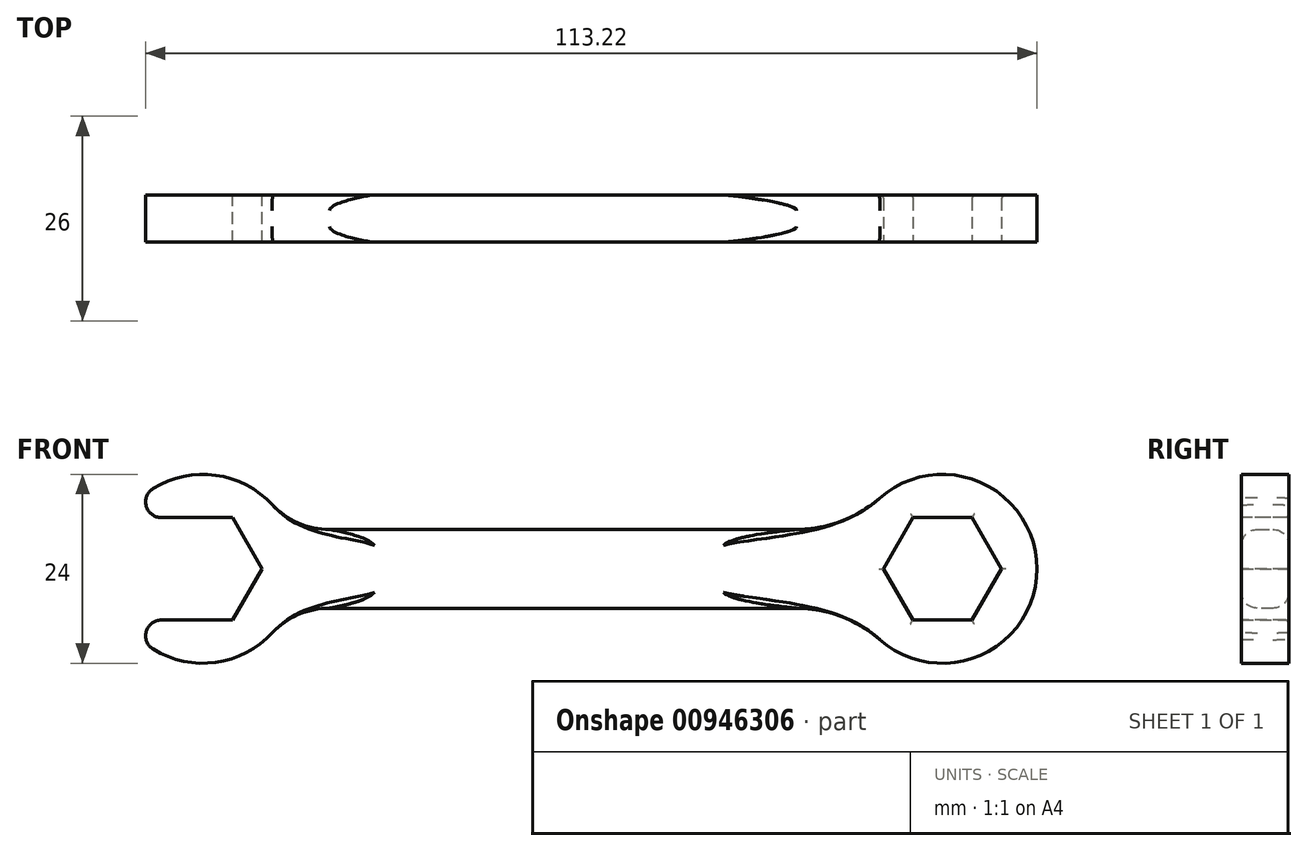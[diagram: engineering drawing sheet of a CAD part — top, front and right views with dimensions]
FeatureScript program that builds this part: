
annotation { "Feature Type Name" : "Feature", "Feature Type Description" : "" }
export const myFeature = defineFeature(function(context is Context, id is Id, definition is map)
    precondition{}
    {
        {
            var Q0;
            Q0=qCreatedBy(makeId("Front.planeOp"),FACE);
            var sketch = newSketch(context, id + "F0", { "sketchPlane" : qUnion([Q0])});
            skArc(sketch, "E0", {"start": v(-10.09, -6.5) * mm, "mid": v(12, 0) * mm, "end": v(-10.09, 6.5) * mm});
            skCircle(sketch, "E1.cCircle", {"center": v(0, 0) * mm, "radius": 6.5 * mm, "construction": true});
            skLineSegment(sketch, "E1.0", {"start": v(-3.75, 6.5) * mm, "end": v(3.75, 6.5) * mm});
            skLineSegment(sketch, "E1.1", {"start": v(3.75, 6.5) * mm, "end": v(7.5, 0) * mm});
            skLineSegment(sketch, "E1.2", {"start": v(7.5, 0) * mm, "end": v(3.75, -6.5) * mm});
            skLineSegment(sketch, "E1.3", {"start": v(3.75, -6.5) * mm, "end": v(-3.75, -6.5) * mm});
            skPoint(sketch, "E1.0.midPoint", {"position": v(0, 6.5) * mm});
            skLineSegment(sketch, "E2.bottom", {"start": v(10.9, 5) * mm, "end": v(105.9, 5) * mm});
            skLineSegment(sketch, "E2.top", {"start": v(10.9, -5) * mm, "end": v(105.9, -5) * mm});
            skLineSegment(sketch, "E2.left", {"start": v(10.9, 5) * mm, "end": v(10.9, -5) * mm});
            skLineSegment(sketch, "E2.right", {"start": v(105.9, 5) * mm, "end": v(105.9, -5) * mm});
            skLineSegment(sketch, "E3", {"start": v(-3.75, 6.5) * mm, "end": v(-10.09, 6.5) * mm});
            skLineSegment(sketch, "E4", {"start": v(-3.75, -6.5) * mm, "end": v(-10.09, -6.5) * mm});
            skSolve(sketch);
        }
        {
            var Q0;
            Q0=makeQuery(id+"F0.imprint","IMPRINT",FACE,{"disambiguationData":[TD([[makeQuery(id+"F0.imprint","IMPRINT",EDGE,{"derivedFrom":sQuery(id+"F0.wireOp",EDGE,"E1.0")}),1.0]])]});
            var Q1;
            {var subQ0=sQuery(id+"F0.wireOp",EDGE,"E2.left");Q1=makeQuery(id+"F0.imprint","IMPRINT",FACE,{"disambiguationData":[TD([[makeQuery(id+"F0.imprint","IMPRINT",EDGE,{"derivedFrom":subQ0}),1.0]])]});}
            var Q2;
            {var subQ1=sQuery(id+"F0.wireOp",EDGE,"E2.bottom");Q2=makeQuery(id+"F0.imprint","IMPRINT",FACE,{"disambiguationData":[TD([[makeQuery(id+"F0.imprint","IMPRINT",EDGE,{"derivedFrom":subQ1}),-1.0]])]});}
            extrude(context, id + "F1", {"entities" : qUnion([Q0, Q1, Q2]), "depth" : 6 * mm, "offsetDistance" : 25 * mm});
        }
        {
            var Q0;
            Q0=makeQuery(id+"F1.opExtrude","SWEPT_EDGE",EDGE,{"disambiguationData":[OSD([sQuery(id+"F0.wireOp",EDGE,"E0"),sQuery(id+"F0.wireOp",EDGE,"E3")])]});
            var Q1;
            Q1=makeQuery(id+"F1.opExtrude","SWEPT_EDGE",EDGE,{"disambiguationData":[OSD([sQuery(id+"F0.wireOp",EDGE,"E0"),sQuery(id+"F0.wireOp",EDGE,"E4")])]});
            fillet(context, id + "F2", {"entities" : qUnion([Q0, Q1]), "radius" : 2 * mm, "tangentPropagation" : true, "allowEdgeOverflow" : false});
        }
        {
            var Q0;
            Q0=makeQuery(id+"F1.opExtrude","SWEPT_EDGE",EDGE,{"disambiguationData":[OSD([sQuery(id+"F0.wireOp",EDGE,"E2.bottom"),sQuery(id+"F0.wireOp",EDGE,"E2.right")])]});
            var Q1;
            Q1=makeQuery(id+"F1.opExtrude","SWEPT_EDGE",EDGE,{"disambiguationData":[OSD([sQuery(id+"F0.wireOp",EDGE,"E2.top"),sQuery(id+"F0.wireOp",EDGE,"E2.right")])]});
            fillet(context, id + "F3", {"entities" : qUnion([Q0, Q1]), "radius" : 5 * mm, "tangentPropagation" : true, "allowEdgeOverflow" : false});
        }
        {
            var Q0;
            Q0=makeQuery(id+"F1.opExtrude","CAP_EDGE",EDGE,{"disambiguationData":[OSD([sQuery(id+"F0.wireOp",EDGE,"E2.bottom")])],"isStart":true});
            var Q1;
            Q1=makeQuery(id+"F1.opExtrude","CAP_EDGE",EDGE,{"disambiguationData":[OSD([sQuery(id+"F0.wireOp",EDGE,"E2.bottom")])],"isStart":false});
            fillet(context, id + "F4", {"entities" : qUnion([Q0, Q1]), "radius" : 2 * mm, "tangentPropagation" : true, "allowEdgeOverflow" : false});
        }
        {
            var Q0;
            Q0=makeQuery(id+"F1.opExtrude","SWEPT_EDGE",EDGE,{"disambiguationData":[OSD([sQuery(id+"F0.wireOp",EDGE,"E0"),sQuery(id+"F0.wireOp",EDGE,"E2.top"),sQuery(id+"F0.wireOp",EDGE,"E2.left")])]});
            var Q1;
            Q1=makeQuery(id+"F1.opExtrude","SWEPT_EDGE",EDGE,{"disambiguationData":[OSD([sQuery(id+"F0.wireOp",EDGE,"E0"),sQuery(id+"F0.wireOp",EDGE,"E2.bottom"),sQuery(id+"F0.wireOp",EDGE,"E2.left")])]});
            fillet(context, id + "F5", {"entities" : qUnion([Q0, Q1]), "radius" : 10 * mm, "tangentPropagation" : true, "allowEdgeOverflow" : false});
        }
        {
            var Q0;
            Q0=makeQuery(id+"F1.opExtrude","CAP_FACE",FACE,{"disambiguationData":[OSD([sQuery(id+"F0.wireOp",EDGE,"E0"),sQuery(id+"F0.wireOp",EDGE,"E1.0"),sQuery(id+"F0.wireOp",EDGE,"E1.1"),sQuery(id+"F0.wireOp",EDGE,"E1.2"),sQuery(id+"F0.wireOp",EDGE,"E1.3"),sQuery(id+"F0.wireOp",EDGE,"E2.bottom"),sQuery(id+"F0.wireOp",EDGE,"E2.top"),sQuery(id+"F0.wireOp",EDGE,"E2.right"),sQuery(id+"F0.wireOp",EDGE,"E3"),sQuery(id+"F0.wireOp",EDGE,"E4")])],"isStart":false});
            var sketch = newSketch(context, id + "F6", { "sketchPlane" : qUnion([Q0])});
            skCircle(sketch, "E5", {"center": v(93.95, 0) * mm, "radius": 12 * mm});
            skSolve(sketch);
        }
        {
            var Q0;
            {var subQ1=sQuery(id+"F0.wireOp",EDGE,"E2.right");var subQ2=sQuery(id+"F0.wireOp",EDGE,"E2.top");var subQ3=sQuery(id+"F0.wireOp",EDGE,"E2.bottom");var subQ4=makeQuery(id+"F1.opExtrude","CAP_FACE",FACE,{"disambiguationData":[OSD([sQuery(id+"F0.wireOp",EDGE,"E0"),sQuery(id+"F0.wireOp",EDGE,"E1.0"),sQuery(id+"F0.wireOp",EDGE,"E1.1"),sQuery(id+"F0.wireOp",EDGE,"E1.2"),sQuery(id+"F0.wireOp",EDGE,"E1.3"),subQ3,subQ2,subQ1,sQuery(id+"F0.wireOp",EDGE,"E3"),sQuery(id+"F0.wireOp",EDGE,"E4")])],"isStart":false});var subQ5=subQ4;var subQ10=makeQuery(id+"F4.opFillet","BLEND_EDGE",EDGE,{"blendedFrom":[makeQuery(id+"F3.opFillet","BLEND_EDGE",EDGE,{"blendedFrom":[makeQuery(id+"F1.opExtrude","SWEPT_EDGE",EDGE,{"disambiguationData":[OSD([subQ3,subQ1])]}),subQ4],"blendedInto":[subQ4]}),subQ5],"blendedInto":[subQ5]});Q0=makeQuery(id+"F6.imprint","IMPRINT",FACE,{"disambiguationData":[TD([[makeQuery(id+"F6.imprint","IMPRINT",EDGE,{"derivedFrom":subQ10}),-1.0]])]});}
            extrude(context, id + "F7", {"entities" : qUnion([Q0]), "operationType" : NewBodyOperationType.ADD, "oppositeDirection" : true, "depth" : 6 * mm, "offsetDistance" : 25 * mm});
        }
        {
            var Q0;
            {var subQ0=sQuery(id+"F0.wireOp",EDGE,"E4");var subQ1=sQuery(id+"F0.wireOp",EDGE,"E3");var subQ2=sQuery(id+"F0.wireOp",EDGE,"E2.right");var subQ3=sQuery(id+"F0.wireOp",EDGE,"E2.top");var subQ4=sQuery(id+"F0.wireOp",EDGE,"E2.bottom");var subQ5=sQuery(id+"F0.wireOp",EDGE,"E1.3");var subQ6=sQuery(id+"F0.wireOp",EDGE,"E1.2");var subQ7=sQuery(id+"F0.wireOp",EDGE,"E1.1");var subQ8=sQuery(id+"F0.wireOp",EDGE,"E1.0");var subQ9=sQuery(id+"F0.wireOp",EDGE,"E0");Q0=makeQuery(id+"F7.boolean.opBoolean","MERGE",FACE,{"derivedFrom":[makeQuery(id+"F1.opExtrude","CAP_FACE",FACE,{"disambiguationData":[OSD([subQ9,subQ8,subQ7,subQ6,subQ5,subQ4,subQ3,subQ2,subQ1,subQ0])],"isStart":false}),makeQuery(id+"F7.opExtrude","CAP_FACE",FACE,{"disambiguationData":[OSD([subQ9,subQ8,subQ7,subQ6,subQ5,subQ4,subQ3,subQ2,subQ1,subQ0,sQuery(id+"F6.wireOp",EDGE,"E5")])],"isStart":true})]});}
            var sketch = newSketch(context, id + "F8", { "sketchPlane" : qUnion([Q0])});
            skCircle(sketch, "E6.cCircle", {"center": v(93.95, 0) * mm, "radius": 6.5 * mm, "construction": true});
            skLineSegment(sketch, "E6.0", {"start": v(90.2, 6.5) * mm, "end": v(97.7, 6.5) * mm});
            skLineSegment(sketch, "E6.1", {"start": v(97.7, 6.5) * mm, "end": v(101.46, 0) * mm});
            skLineSegment(sketch, "E6.2", {"start": v(101.46, 0) * mm, "end": v(97.7, -6.5) * mm});
            skLineSegment(sketch, "E6.3", {"start": v(97.7, -6.5) * mm, "end": v(90.2, -6.5) * mm});
            skLineSegment(sketch, "E6.4", {"start": v(90.2, -6.5) * mm, "end": v(86.45, 0) * mm});
            skLineSegment(sketch, "E6.5", {"start": v(86.45, 0) * mm, "end": v(90.2, 6.5) * mm});
            skPoint(sketch, "E6.0.midPoint", {"position": v(93.95, 6.5) * mm});
            skSolve(sketch);
        }
        {
            var Q0;
            Q0=makeQuery(id+"F8.imprint","IMPRINT",FACE,{"disambiguationData":[TD([[makeQuery(id+"F8.imprint","IMPRINT",EDGE,{"derivedFrom":sQuery(id+"F8.wireOp",EDGE,"E6.0")}),-1.0]])]});
            extrude(context, id + "F9", {"entities" : qUnion([Q0]), "operationType" : NewBodyOperationType.REMOVE, "endBound" : BoundingType.THROUGH_ALL, "oppositeDirection" : true, "depth" : 25 * mm, "offsetDistance" : 25 * mm});
        }
        {
            var Q0;
            Q0=makeQuery(id+"F9.boolean.opBoolean","COPY",EDGE,{"derivedFrom":makeQuery(id+"F9.opExtrude","CAP_EDGE",EDGE,{"disambiguationData":[OSD([sQuery(id+"F8.wireOp",EDGE,"E6.5")])],"isStart":true})});
            var Q1;
            Q1=makeQuery(id+"F9.boolean.opBoolean","COPY",EDGE,{"derivedFrom":makeQuery(id+"F9.opExtrude","CAP_EDGE",EDGE,{"disambiguationData":[OSD([sQuery(id+"F8.wireOp",EDGE,"E6.0")])],"isStart":true})});
            var Q2;
            Q2=makeQuery(id+"F9.boolean.opBoolean","COPY",EDGE,{"derivedFrom":makeQuery(id+"F9.opExtrude","CAP_EDGE",EDGE,{"disambiguationData":[OSD([sQuery(id+"F8.wireOp",EDGE,"E6.1")])],"isStart":true})});
            var Q3;
            Q3=makeQuery(id+"F9.boolean.opBoolean","COPY",EDGE,{"derivedFrom":makeQuery(id+"F9.opExtrude","CAP_EDGE",EDGE,{"disambiguationData":[OSD([sQuery(id+"F8.wireOp",EDGE,"E6.2")])],"isStart":true})});
            var Q4;
            Q4=makeQuery(id+"F9.boolean.opBoolean","COPY",EDGE,{"derivedFrom":makeQuery(id+"F9.opExtrude","CAP_EDGE",EDGE,{"disambiguationData":[OSD([sQuery(id+"F8.wireOp",EDGE,"E6.3")])],"isStart":true})});
            var Q5;
            Q5=makeQuery(id+"F9.boolean.opBoolean","COPY",EDGE,{"derivedFrom":makeQuery(id+"F9.opExtrude","CAP_EDGE",EDGE,{"disambiguationData":[OSD([sQuery(id+"F8.wireOp",EDGE,"E6.4")])],"isStart":true})});
            var Q6;
            {var subQ0=sQuery(id+"F0.wireOp",EDGE,"E4");var subQ1=sQuery(id+"F0.wireOp",EDGE,"E3");var subQ2=sQuery(id+"F0.wireOp",EDGE,"E2.right");var subQ3=sQuery(id+"F0.wireOp",EDGE,"E2.top");var subQ4=sQuery(id+"F0.wireOp",EDGE,"E2.bottom");var subQ5=sQuery(id+"F0.wireOp",EDGE,"E1.3");var subQ6=sQuery(id+"F0.wireOp",EDGE,"E1.2");var subQ7=sQuery(id+"F0.wireOp",EDGE,"E1.1");var subQ8=sQuery(id+"F0.wireOp",EDGE,"E1.0");var subQ9=sQuery(id+"F0.wireOp",EDGE,"E0");Q6=makeQuery(id+"F9.boolean.opBoolean","INTERSECT",EDGE,{"derivedFrom":[makeQuery(id+"F7.boolean.opBoolean","MERGE",FACE,{"derivedFrom":[makeQuery(id+"F1.opExtrude","CAP_FACE",FACE,{"disambiguationData":[OSD([subQ9,subQ8,subQ7,subQ6,subQ5,subQ4,subQ3,subQ2,subQ1,subQ0])],"isStart":true}),makeQuery(id+"F7.opExtrude","CAP_FACE",FACE,{"disambiguationData":[OSD([subQ9,subQ8,subQ7,subQ6,subQ5,subQ4,subQ3,subQ2,subQ1,subQ0,sQuery(id+"F6.wireOp",EDGE,"E5")])],"isStart":false})]}),makeQuery(id+"F9.opExtrude","SWEPT_FACE",FACE,{"disambiguationData":[OSD([sQuery(id+"F8.wireOp",EDGE,"E6.0")])]})]});}
            var Q7;
            {var subQ0=sQuery(id+"F0.wireOp",EDGE,"E4");var subQ1=sQuery(id+"F0.wireOp",EDGE,"E3");var subQ2=sQuery(id+"F0.wireOp",EDGE,"E2.right");var subQ3=sQuery(id+"F0.wireOp",EDGE,"E2.top");var subQ4=sQuery(id+"F0.wireOp",EDGE,"E2.bottom");var subQ5=sQuery(id+"F0.wireOp",EDGE,"E1.3");var subQ6=sQuery(id+"F0.wireOp",EDGE,"E1.2");var subQ7=sQuery(id+"F0.wireOp",EDGE,"E1.1");var subQ8=sQuery(id+"F0.wireOp",EDGE,"E1.0");var subQ9=sQuery(id+"F0.wireOp",EDGE,"E0");Q7=makeQuery(id+"F9.boolean.opBoolean","INTERSECT",EDGE,{"derivedFrom":[makeQuery(id+"F7.boolean.opBoolean","MERGE",FACE,{"derivedFrom":[makeQuery(id+"F1.opExtrude","CAP_FACE",FACE,{"disambiguationData":[OSD([subQ9,subQ8,subQ7,subQ6,subQ5,subQ4,subQ3,subQ2,subQ1,subQ0])],"isStart":true}),makeQuery(id+"F7.opExtrude","CAP_FACE",FACE,{"disambiguationData":[OSD([subQ9,subQ8,subQ7,subQ6,subQ5,subQ4,subQ3,subQ2,subQ1,subQ0,sQuery(id+"F6.wireOp",EDGE,"E5")])],"isStart":false})]}),makeQuery(id+"F9.opExtrude","SWEPT_FACE",FACE,{"disambiguationData":[OSD([sQuery(id+"F8.wireOp",EDGE,"E6.5")])]})]});}
            var Q8;
            {var subQ0=sQuery(id+"F0.wireOp",EDGE,"E4");var subQ1=sQuery(id+"F0.wireOp",EDGE,"E3");var subQ2=sQuery(id+"F0.wireOp",EDGE,"E2.right");var subQ3=sQuery(id+"F0.wireOp",EDGE,"E2.top");var subQ4=sQuery(id+"F0.wireOp",EDGE,"E2.bottom");var subQ5=sQuery(id+"F0.wireOp",EDGE,"E1.3");var subQ6=sQuery(id+"F0.wireOp",EDGE,"E1.2");var subQ7=sQuery(id+"F0.wireOp",EDGE,"E1.1");var subQ8=sQuery(id+"F0.wireOp",EDGE,"E1.0");var subQ9=sQuery(id+"F0.wireOp",EDGE,"E0");Q8=makeQuery(id+"F9.boolean.opBoolean","INTERSECT",EDGE,{"derivedFrom":[makeQuery(id+"F7.boolean.opBoolean","MERGE",FACE,{"derivedFrom":[makeQuery(id+"F1.opExtrude","CAP_FACE",FACE,{"disambiguationData":[OSD([subQ9,subQ8,subQ7,subQ6,subQ5,subQ4,subQ3,subQ2,subQ1,subQ0])],"isStart":true}),makeQuery(id+"F7.opExtrude","CAP_FACE",FACE,{"disambiguationData":[OSD([subQ9,subQ8,subQ7,subQ6,subQ5,subQ4,subQ3,subQ2,subQ1,subQ0,sQuery(id+"F6.wireOp",EDGE,"E5")])],"isStart":false})]}),makeQuery(id+"F9.opExtrude","SWEPT_FACE",FACE,{"disambiguationData":[OSD([sQuery(id+"F8.wireOp",EDGE,"E6.4")])]})]});}
            var Q9;
            {var subQ0=sQuery(id+"F0.wireOp",EDGE,"E4");var subQ1=sQuery(id+"F0.wireOp",EDGE,"E3");var subQ2=sQuery(id+"F0.wireOp",EDGE,"E2.right");var subQ3=sQuery(id+"F0.wireOp",EDGE,"E2.top");var subQ4=sQuery(id+"F0.wireOp",EDGE,"E2.bottom");var subQ5=sQuery(id+"F0.wireOp",EDGE,"E1.3");var subQ6=sQuery(id+"F0.wireOp",EDGE,"E1.2");var subQ7=sQuery(id+"F0.wireOp",EDGE,"E1.1");var subQ8=sQuery(id+"F0.wireOp",EDGE,"E1.0");var subQ9=sQuery(id+"F0.wireOp",EDGE,"E0");Q9=makeQuery(id+"F9.boolean.opBoolean","INTERSECT",EDGE,{"derivedFrom":[makeQuery(id+"F7.boolean.opBoolean","MERGE",FACE,{"derivedFrom":[makeQuery(id+"F1.opExtrude","CAP_FACE",FACE,{"disambiguationData":[OSD([subQ9,subQ8,subQ7,subQ6,subQ5,subQ4,subQ3,subQ2,subQ1,subQ0])],"isStart":true}),makeQuery(id+"F7.opExtrude","CAP_FACE",FACE,{"disambiguationData":[OSD([subQ9,subQ8,subQ7,subQ6,subQ5,subQ4,subQ3,subQ2,subQ1,subQ0,sQuery(id+"F6.wireOp",EDGE,"E5")])],"isStart":false})]}),makeQuery(id+"F9.opExtrude","SWEPT_FACE",FACE,{"disambiguationData":[OSD([sQuery(id+"F8.wireOp",EDGE,"E6.3")])]})]});}
            var Q10;
            {var subQ0=sQuery(id+"F0.wireOp",EDGE,"E4");var subQ1=sQuery(id+"F0.wireOp",EDGE,"E3");var subQ2=sQuery(id+"F0.wireOp",EDGE,"E2.right");var subQ3=sQuery(id+"F0.wireOp",EDGE,"E2.top");var subQ4=sQuery(id+"F0.wireOp",EDGE,"E2.bottom");var subQ5=sQuery(id+"F0.wireOp",EDGE,"E1.3");var subQ6=sQuery(id+"F0.wireOp",EDGE,"E1.2");var subQ7=sQuery(id+"F0.wireOp",EDGE,"E1.1");var subQ8=sQuery(id+"F0.wireOp",EDGE,"E1.0");var subQ9=sQuery(id+"F0.wireOp",EDGE,"E0");Q10=makeQuery(id+"F9.boolean.opBoolean","INTERSECT",EDGE,{"derivedFrom":[makeQuery(id+"F7.boolean.opBoolean","MERGE",FACE,{"derivedFrom":[makeQuery(id+"F1.opExtrude","CAP_FACE",FACE,{"disambiguationData":[OSD([subQ9,subQ8,subQ7,subQ6,subQ5,subQ4,subQ3,subQ2,subQ1,subQ0])],"isStart":true}),makeQuery(id+"F7.opExtrude","CAP_FACE",FACE,{"disambiguationData":[OSD([subQ9,subQ8,subQ7,subQ6,subQ5,subQ4,subQ3,subQ2,subQ1,subQ0,sQuery(id+"F6.wireOp",EDGE,"E5")])],"isStart":false})]}),makeQuery(id+"F9.opExtrude","SWEPT_FACE",FACE,{"disambiguationData":[OSD([sQuery(id+"F8.wireOp",EDGE,"E6.2")])]})]});}
            var Q11;
            {var subQ0=sQuery(id+"F0.wireOp",EDGE,"E4");var subQ1=sQuery(id+"F0.wireOp",EDGE,"E3");var subQ2=sQuery(id+"F0.wireOp",EDGE,"E2.right");var subQ3=sQuery(id+"F0.wireOp",EDGE,"E2.top");var subQ4=sQuery(id+"F0.wireOp",EDGE,"E2.bottom");var subQ5=sQuery(id+"F0.wireOp",EDGE,"E1.3");var subQ6=sQuery(id+"F0.wireOp",EDGE,"E1.2");var subQ7=sQuery(id+"F0.wireOp",EDGE,"E1.1");var subQ8=sQuery(id+"F0.wireOp",EDGE,"E1.0");var subQ9=sQuery(id+"F0.wireOp",EDGE,"E0");Q11=makeQuery(id+"F9.boolean.opBoolean","INTERSECT",EDGE,{"derivedFrom":[makeQuery(id+"F7.boolean.opBoolean","MERGE",FACE,{"derivedFrom":[makeQuery(id+"F1.opExtrude","CAP_FACE",FACE,{"disambiguationData":[OSD([subQ9,subQ8,subQ7,subQ6,subQ5,subQ4,subQ3,subQ2,subQ1,subQ0])],"isStart":true}),makeQuery(id+"F7.opExtrude","CAP_FACE",FACE,{"disambiguationData":[OSD([subQ9,subQ8,subQ7,subQ6,subQ5,subQ4,subQ3,subQ2,subQ1,subQ0,sQuery(id+"F6.wireOp",EDGE,"E5")])],"isStart":false})]}),makeQuery(id+"F9.opExtrude","SWEPT_FACE",FACE,{"disambiguationData":[OSD([sQuery(id+"F8.wireOp",EDGE,"E6.1")])]})]});}
            fillet(context, id + "F10", {"entities" : qUnion([Q0, Q1, Q2, Q3, Q4, Q5, Q6, Q7, Q8, Q9, Q10, Q11]), "radius" : .5 * mm, "tangentPropagation" : true, "allowEdgeOverflow" : false});
        }
        {
            var Q0;
            Q0=makeQuery(id+"F7.boolean.opBoolean","INTERSECT",EDGE,{"derivedFrom":[makeQuery(id+"F1.opExtrude","SWEPT_FACE",FACE,{"disambiguationData":[OSD([sQuery(id+"F0.wireOp",EDGE,"E2.top")])]}),makeQuery(id+"F7.opExtrude","SWEPT_FACE",FACE,{"disambiguationData":[OSD([sQuery(id+"F6.wireOp",EDGE,"E5")])]})]});
            var Q1;
            Q1=makeQuery(id+"F7.boolean.opBoolean","INTERSECT",EDGE,{"derivedFrom":[makeQuery(id+"F1.opExtrude","SWEPT_FACE",FACE,{"disambiguationData":[OSD([sQuery(id+"F0.wireOp",EDGE,"E2.bottom")])]}),makeQuery(id+"F7.opExtrude","SWEPT_FACE",FACE,{"disambiguationData":[OSD([sQuery(id+"F6.wireOp",EDGE,"E5")])]})]});
            fillet(context, id + "F11", {"entities" : qUnion([Q0, Q1]), "radius" : 16 * mm, "tangentPropagation" : true, "allowEdgeOverflow" : false});
        }
    });
